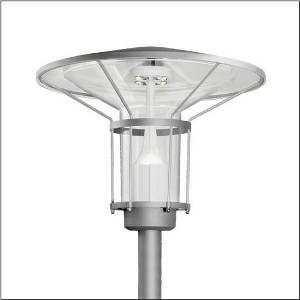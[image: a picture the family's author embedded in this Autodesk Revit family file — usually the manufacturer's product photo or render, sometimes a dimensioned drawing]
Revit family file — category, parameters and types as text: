
# Revit family: laterne_classic_iq___pl1_2s_5xa5245jf14h000022_9e24
name_source: partatom
category: Lighting Fixtures
units: mm (PartAtom-declared; Revit-internal decimal feet)

## family parameters
Cut with Voids When Loaded = No
Host = Face
Light Source = No
Part Type = Normal
Room Calculation Point = No
Round Connector Dimension = Use Diameter
Shared = No

## types (1)
- --- (1 x LED, 2660 lm, 19.3 W, 3000K)
    Apparent Load = 19 VA
    CIE Flux Codes = 21 60 93 97 100
    Color Rendering = 70
    Color Temperature = 3000K
    Default Elevation = 1800 mm
    Description = Lantern Classic iQ, mast luminaire, Module 540 iQ-SR, primary light control with 3 zone facetted reflector, of plastic, silver coated, highly specular, structured, primary optical cover: cover, of PMMA, transparent, light distribution: PL1.2s, light emission: direct distribution, primary light characteristic: symmetric, installation type: post-top, LED, High Power LED, rated luminous flux: 2.660lm, luminous efficacy: 138lm/W, light colour: 730, colour temperature: 3000K, control gear: iQ Street-Remote, control: Street-Remote, Auto-Match, Temp-Guard, Lumen-Switch, Night-Set, Smart-Wire, Light-Fading, Desk-Remote (wireless, voltage-free reading and setting of iQ features in the workshop via application-optimized NFC function/RFID function), optimised constant luminous flux control (CLO 2.0), pre-setting: logarithmic dimming characteristic, mains connection: 230..240V, AC, 50/60Hz, connection cable pre-assembled, cable length: 5,5m, wiring characteristics: H07RN-F, start of lifetime: 19W, end of service life: 21W, reduction: 10W, luminaire housing, upper part, of glass-fibre reinforced polyester, coated, Siteco® metallic grey (DB 702S), diameter: 750mm, height: 596mm, spigot size: d x l = 76 x 70mm (post-top) | with reducer (optional accessory) 60 x 70mm, mounting height: 3..5m, post-top mast mounting element, of diecast aluminium, coated, Siteco® metallic grey (DB 702S), Module 540 iQ-SR, traffic white (RAL 9016), equipment: standard, protection rating (complete): IP65, insulation class (complete): insulation class II (safety insulation), certification: CE, ENEC, VDE, packaging unit: 1 piece

Light Distribution: PL1.2s
    Height = 596 mm
    Lamp = 1 x LED
    Lamp Light Flux = 2660 lm
    Lamp Power = 19.3 W
    Lamp count = 1
    Length = 750 mm
    Luminous efficacy = 138 lm/W
    Manufacturer = Siteco
    ModVariant = No
    Model = 5XA5245JF14H000022
    Number of Poles = 1
    OnlyDefault = Yes
    Power Factor = 1
    Product Name = Laterne Classic iQ | PL1.2s
    Product group = mast luminaire | pylon top
    ProductGroupID = 6100
    Protection Class = Protection class II
    Protection Degree = IP 65
    RLX_Detail_Level = 1
    RLX_Emergency_Light_Flux = 0 lm
    RLX_Emergency_Type = 0
    RLX_Emergency_Type_DB = No
    RlxData = <blob elided: 37829 chars, md5=07061e7c>
    Socket = socket
    Standby Power = 0 W
    System Light Flux = 2660 lm
    System Power = 19 W
    Type Comments = factory setting: luminous flux: 100 % | dim-lin: 254 | 403 mA
    Type Image = l_1006052.jpg
    URL = http://relux.com
    VarID = @adj_167147
    Voltage = 0 V
    Weight = 0.00 kg
    Width = 0 mm  [stored 0 ft]

note: [stored X ft] marks values corroborated as IEEE doubles in the binary element streams (Revit-internal decimal feet)

## geometry (parser evidence)
native form markers: Blend x4, Sweep x11
no freeform markers — native parametric forms only
